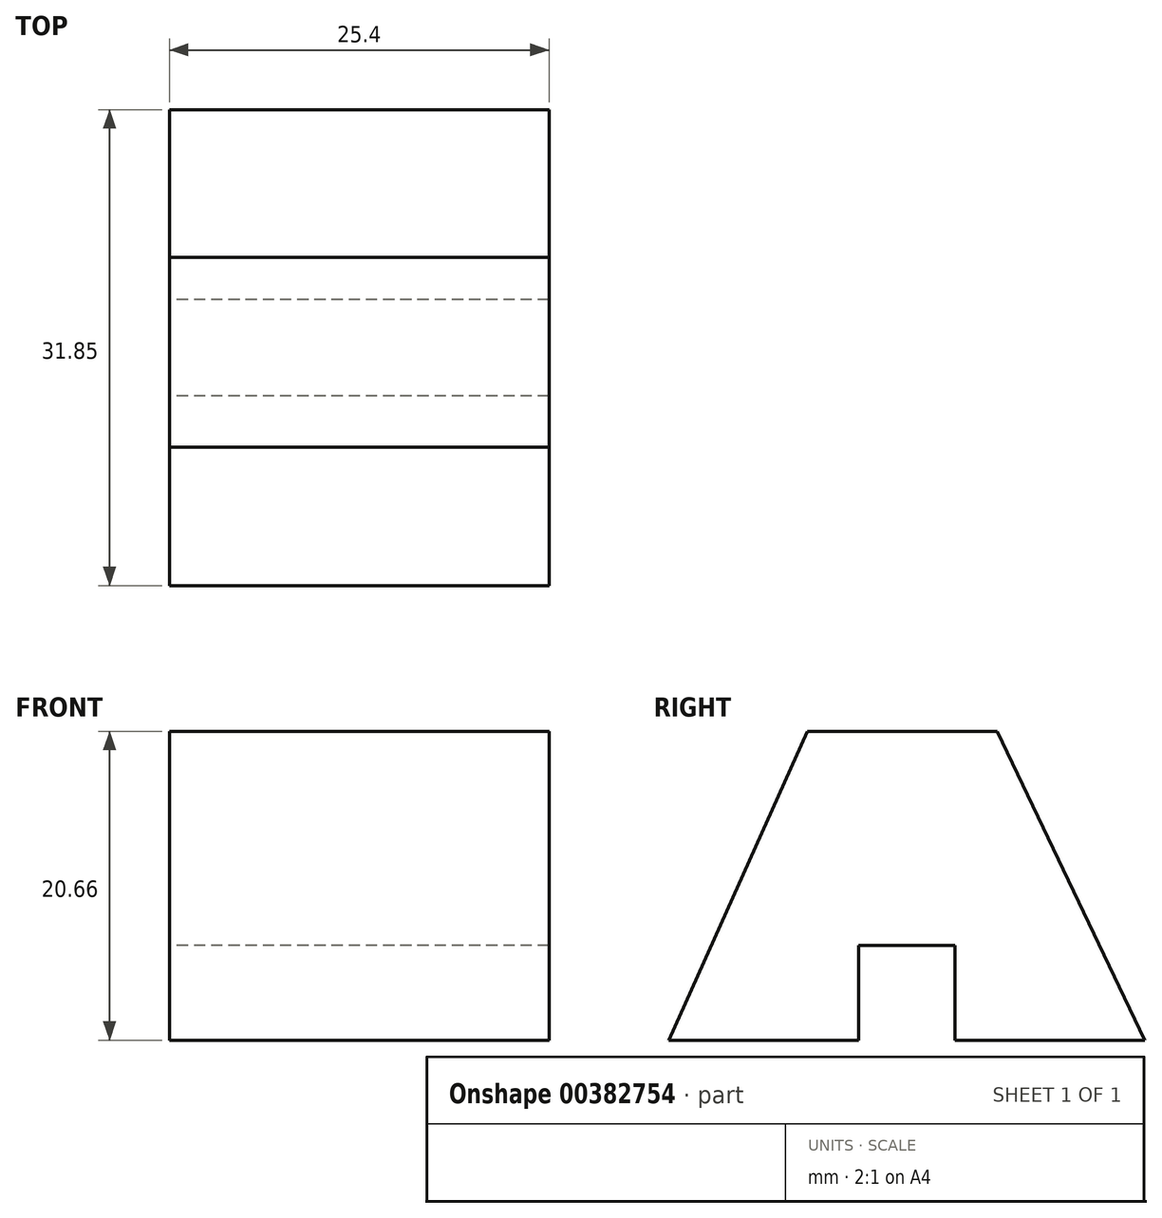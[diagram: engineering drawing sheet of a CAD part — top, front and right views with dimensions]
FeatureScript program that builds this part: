
annotation { "Feature Type Name" : "Feature", "Feature Type Description" : "" }
export const myFeature = defineFeature(function(context is Context, id is Id, definition is map)
    precondition{}
    {
        {
            var Q0;
            Q0=qCreatedBy(makeId("Front.planeOp"),FACE);
            var sketch = newSketch(context, id + "F0", { "sketchPlane" : qUnion([Q0])});
            skSolve(sketch);
        }
        {
            var Q0;
            Q0=qCreatedBy(makeId("Right.planeOp"),FACE);
            var sketch = newSketch(context, id + "F1", { "sketchPlane" : qUnion([Q0])});
            skLineSegment(sketch, "E0", {"start": v(0, 0) * mm, "end": v(-12.7, 0) * mm});
            skLineSegment(sketch, "E1", {"start": v(-12.7, 0) * mm, "end": v(-3.43, 20.66) * mm});
            skLineSegment(sketch, "E2", {"start": v(0, 0) * mm, "end": v(0, 6.35) * mm});
            skLineSegment(sketch, "E3", {"start": v(0, 6.35) * mm, "end": v(6.45, 6.35) * mm});
            skLineSegment(sketch, "E4", {"start": v(6.45, 6.35) * mm, "end": v(6.45, 0) * mm});
            skLineSegment(sketch, "E5", {"start": v(6.45, 0) * mm, "end": v(19.15, 0) * mm});
            skLineSegment(sketch, "E6", {"start": v(19.15, 0) * mm, "end": v(9.27, 20.66) * mm});
            skLineSegment(sketch, "E7", {"start": v(9.27, 20.66) * mm, "end": v(-3.43, 20.66) * mm});
            skSolve(sketch);
        }
        {
            var Q0;
            Q0 = qSketchRegion(id + "F0", true);
            var Q1;
            Q1 = qSketchRegion(id + "F1", true);
            extrude(context, id + "F2", {"entities" : qUnion([Q0, Q1]), "depth" : 25.4 * mm});
        }
    });
